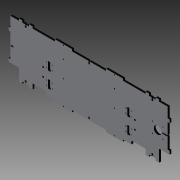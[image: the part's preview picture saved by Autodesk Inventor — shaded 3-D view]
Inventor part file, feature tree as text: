
AUTODESK INVENTOR PART (.ipt)
format: ipt  version: 2013 (Build 170138000, 138)  size: 669,696 bytes
history: native  units: in
note: dims shown in document units (in); Inventor stores cm internally (conversion verified against a paired STEP export)
features: extrude x16, sketch x16, mirror x6, reference x4, fillet x1
ambient origin geometry x8: Origin, YZ Plane, XZ Plane, XY Plane, X Axis, Y Axis, Z Axis, Center Point
bodies: Solid1 (feature_tree)
feature tree (43):
  extrude  "Extrusion1"  Depth=2.7559in
  extrude  "Extrusion2"  Depth=0.2953in
  extrude  "Extrusion3"  Depth=0.1575in
  extrude  "Extrusion4"  Depth=0.5906in
  extrude  "Extrusion5"  Depth=0.1575in
  extrude  "Extrusion6"  Depth=0.1575in
  mirror  "Mirror1"
  mirror  "Mirror2"
  extrude  "Extrusion7"  Depth=18.2283in
  extrude  "Extrusion8"  Depth=0.1181in
  extrude  "Extrusion9"  Depth=0.0787in
  extrude  "Extrusion10"  Depth=0.0787in
  mirror  "Mirror3"
  mirror  "Mirror4"
  fillet  "Fillet1"  Radius=0.225in
  extrude  "Extrusion11"  Depth=2.9528in
  extrude  "Extrusion12"  Depth=0.1181in
  mirror  "Mirror5"
  extrude  "Extrusion13"  Depth=0.225in TaperAngle=0.0deg
  extrude  "Extrusion14"  Depth=0.9843in
  extrude  "Extrusion15"  Depth=0.7874in
  extrude  "Extrusion16"  Depth=0.225in
  mirror  "Mirror6"
  sketch  "Sketch1"  dims[d0=0.225in d1=0.0in d2=2.7559in]
  sketch  "Sketch2"  dims[d4=9.2126in d5=0.2953in]
  sketch  "Sketch3"  dims[d6=0.9449in d7=0.1575in]
  sketch  "Sketch4"  dims[d8=0.0591in d9=0.5906in]
  sketch  "Sketch5"  dims[d10=0.1969in d11=0.1575in d12=0.0591in d13=0.5906in d14=0.1969in]
  reference  "Reference5"
  sketch  "Sketch6"  dims[d15=0.1575in d16=0.0591in d17=0.5906in d18=0.1969in d19=0.1575in d20=0.0591in d21=0.5906in d22=0.1969in]
  reference  "Reference6"
  sketch  "Sketch7"  dims[d23=0.225in d24=0.0in d25=18.2283in]
  sketch  "Sketch8"  dims[d27=5.9055in d31=0.1181in]
  sketch  "Sketch10"  dims[d32=0.2474in d33=0.0787in]
  sketch  "Sketch11"  dims[d34=0.2165in d35=0.0787in d37=0.225in d38=0.0in]
  sketch  "Sketch12"  dims[d39=0.225in d41=2.9528in]
  sketch  "Sketch13"  dims[d42=1.9685in d43=0.1181in]
  sketch  "Sketch14"  dims[d44=0.225in d45=0.0in d46=0.225in d47=0.0in]
  reference  "Reference7"
  sketch  "Sketch15"  dims[d48=0.225in d49=0.0in d50=0.9843in]
  sketch  "Sketch16"  dims[d51=0.225in d52=0.0in d53=0.7874in]
  reference  "Reference8"
  sketch  "Sketch17"  dims[d55=0.3937in d56=0.225in d57=0.225in d58=0.0in d59=0.3937in d62=4.9213in d63=0.225in d64=0.0in d65=0.2165in d67=0.225in d68=0.0in d69=0.0787in d70=1.6535in d71=0.9055in d72=1.2205in d73=0.1181in d74=1.0in d75=0.0in d76=0.7874in d78=0.1969in d79=0.9843in d80=1.0in d81=0.0in d82=5.315in d83=1.0in d84=0.0in d85=0.9843in d86=0.4921in d87=1.0in d88=0.0in d89=1.0in d90=0.0in d91=0.3937in d93=0.3937in d94=0.0591in d95=0.1575in d96=1.5748in d97=2.9528in d98=0.9843in d99=5.9055in d100=1.0in d101=0.0in]
